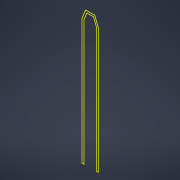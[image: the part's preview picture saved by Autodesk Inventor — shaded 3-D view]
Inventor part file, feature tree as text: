
AUTODESK INVENTOR PART (.ipt)
format: ipt  version: 2022 (Build 260153000, 153)  size: 79,360 bytes
history: native  units: mm
features: other x4, sketch x1, reference x1
ambient origin geometry x8: Origin, YZ Plane, XZ Plane, XY Plane, X Axis, Y Axis, Z Axis, Center Point
feature tree (6):
  sketch  "Sketch1"
  reference  "Reference1"
  other  "RobotPallet.iam"
  other  "EstructuraInferior:1"
  other  "Frame_Base:1"
  other  "ISO 10799-2 40x40x4 - 3515.41:1"
